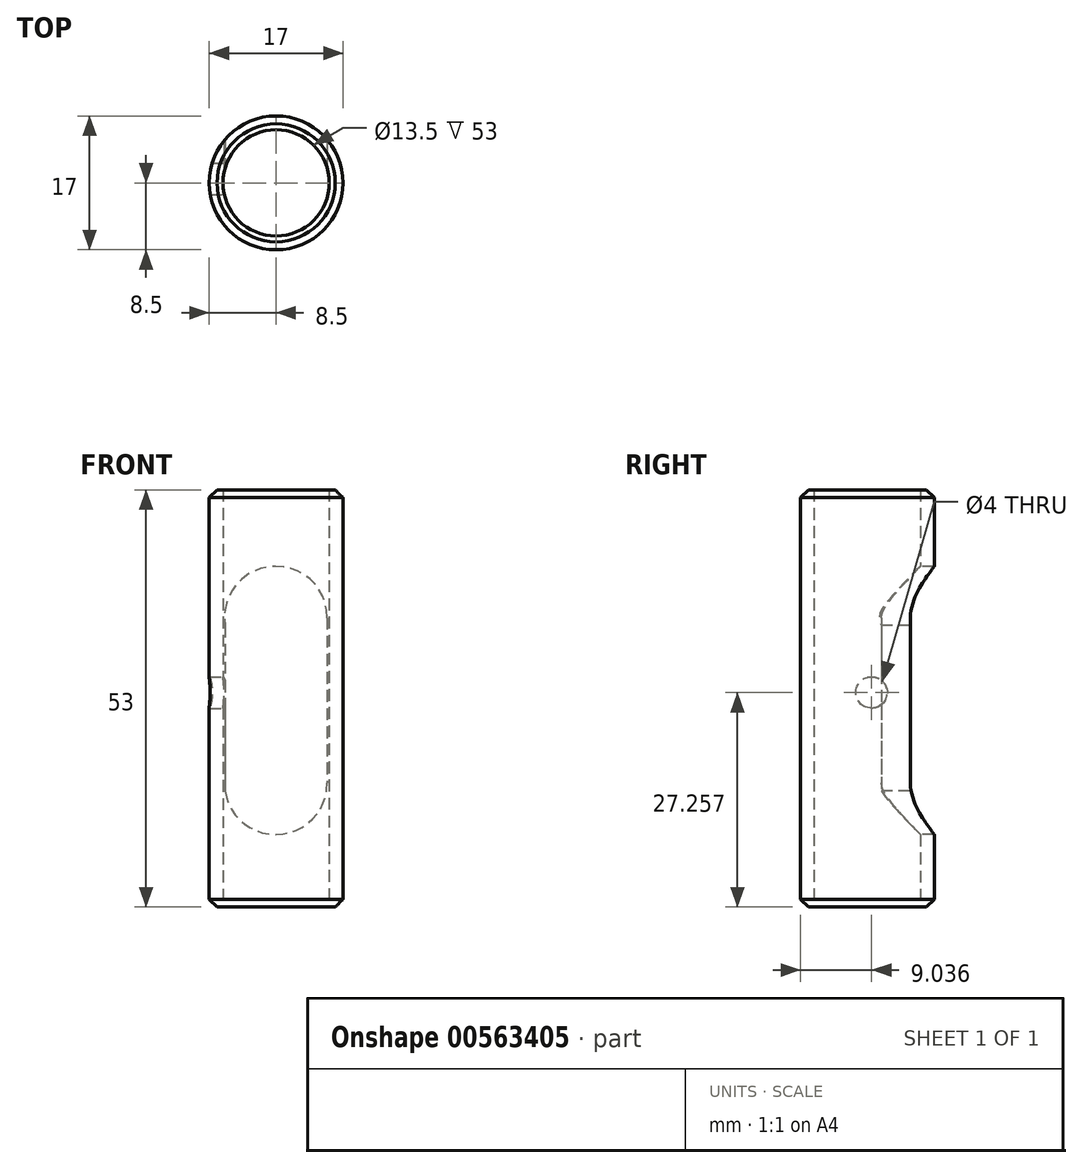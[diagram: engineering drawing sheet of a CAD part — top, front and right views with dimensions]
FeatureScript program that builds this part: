
annotation { "Feature Type Name" : "Feature", "Feature Type Description" : "" }
export const myFeature = defineFeature(function(context is Context, id is Id, definition is map)
    precondition{}
    {
        {
            var Q0;
            Q0=qCreatedBy(makeId("Top.planeOp"),FACE);
            var sketch = newSketch(context, id + "F0", { "sketchPlane" : qUnion([Q0])});
            skCircle(sketch, "E0", {"center": v(0, 0) * mm, "radius": 8.5 * mm});
            skSolve(sketch);
        }
        {
            var Q0;
            Q0 = qSketchRegion(id + "F0", true);
            extrude(context, id + "F1", {"entities" : qUnion([Q0]), "depth" : 53 * mm, "offsetDistance" : 25.4 * mm});
        }
        {
            var Q0;
            Q0=qCreatedBy(makeId("Top.planeOp"),FACE);
            var sketch = newSketch(context, id + "F2", { "sketchPlane" : qUnion([Q0])});
            skPoint(sketch, "E1", {"position": v(0, 0) * mm});
            skSolve(sketch);
        }
        {
            var Q0;
            Q0=sQuery(id+"F2.wireOp",VERTEX,"E1");
            var Q1;
            Q1=makeQuery(id+"F1.opExtrude","SWEPT_BODY",BODY,{"disambiguationData":[OSD([sQuery(id+"F0.wireOp",EDGE,"E0")])]});
            hole(context, id + "F3", {"style" : HoleStyle.SIMPLE, "endStyle" : HoleEndStyle.THROUGH, "oppositeDirection" : true, "holeDiameter" : 13.5 * mm, "isTappedThrough" : true, "tappedDepth" : 12.7 * mm, "tapClearance" : 3, "locations" : qUnion([Q0]), "scope" : qUnion([Q1])});
        }
        {
            var Q0;
            Q0=qCreatedBy(makeId("Front.planeOp"),FACE);
            var sketch = newSketch(context, id + "F4", { "sketchPlane" : qUnion([Q0])});
            skLineSegment(sketch, "E2", {"start": v(6.5, 20.24) * mm, "end": v(6.5, 36.76) * mm});
            skLineSegment(sketch, "E3", {"start": v(-6.5, 35.76) * mm, "end": v(-6.5, 14.76) * mm});
            skLineSegment(sketch, "E4.left", {"start": v(6.5, 36.76) * mm, "end": v(6.5, 15.76) * mm});
            skArc(sketch, "E5", {"start": v(-6.5, 14.76) * mm, "mid": v(0.46, 9.24) * mm, "end": v(6.5, 15.76) * mm});
            skArc(sketch, "E6", {"start": v(6.5, 36.76) * mm, "mid": v(-0.54, 43.27) * mm, "end": v(-6.5, 35.76) * mm});
            skSolve(sketch);
        }
        {
            var Q0;
            Q0 = qSketchRegion(id + "F4", true);
            extrude(context, id + "F5", {"entities" : qUnion([Q0]), "operationType" : NewBodyOperationType.REMOVE, "oppositeDirection" : true, "depth" : 12 * mm, "offsetDistance" : 25.4 * mm});
        }
        {
            var Q0;
            Q0=qCreatedBy(makeId("Right.planeOp"),FACE);
            var sketch = newSketch(context, id + "F6", { "sketchPlane" : qUnion([Q0])});
            skPoint(sketch, "E7", {"position": v(0.54, 27.26) * mm});
            skSolve(sketch);
        }
        {
            var Q0;
            Q0=sQuery(id+"F6.wireOp",VERTEX,"E7");
            var Q1;
            Q1=makeQuery(id+"F1.opExtrude","SWEPT_BODY",BODY,{"disambiguationData":[OSD([sQuery(id+"F0.wireOp",EDGE,"E0")])]});
            hole(context, id + "F7", {"style" : HoleStyle.SIMPLE, "endStyle" : HoleEndStyle.THROUGH, "holeDiameter" : 4 * mm, "isTappedThrough" : true, "tappedDepth" : 12.7 * mm, "tapClearance" : 3, "locations" : qUnion([Q0]), "scope" : qUnion([Q1])});
        }
        {
            var Q0;
            Q0=makeQuery(id+"F1.opExtrude","CAP_EDGE",EDGE,{"disambiguationData":[OSD([sQuery(id+"F0.wireOp",EDGE,"E0")])],"isStart":false});
            chamfer(context, id + "F8", {"entities" : qUnion([Q0]), "width" : 1 * mm, "tangentPropagation" : true});
        }
        {
            var Q0;
            Q0=makeQuery(id+"F1.opExtrude","CAP_EDGE",EDGE,{"disambiguationData":[OSD([sQuery(id+"F0.wireOp",EDGE,"E0")])],"isStart":true});
            chamfer(context, id + "F9", {"entities" : qUnion([Q0]), "width" : 1 * mm, "tangentPropagation" : true});
        }
    });
